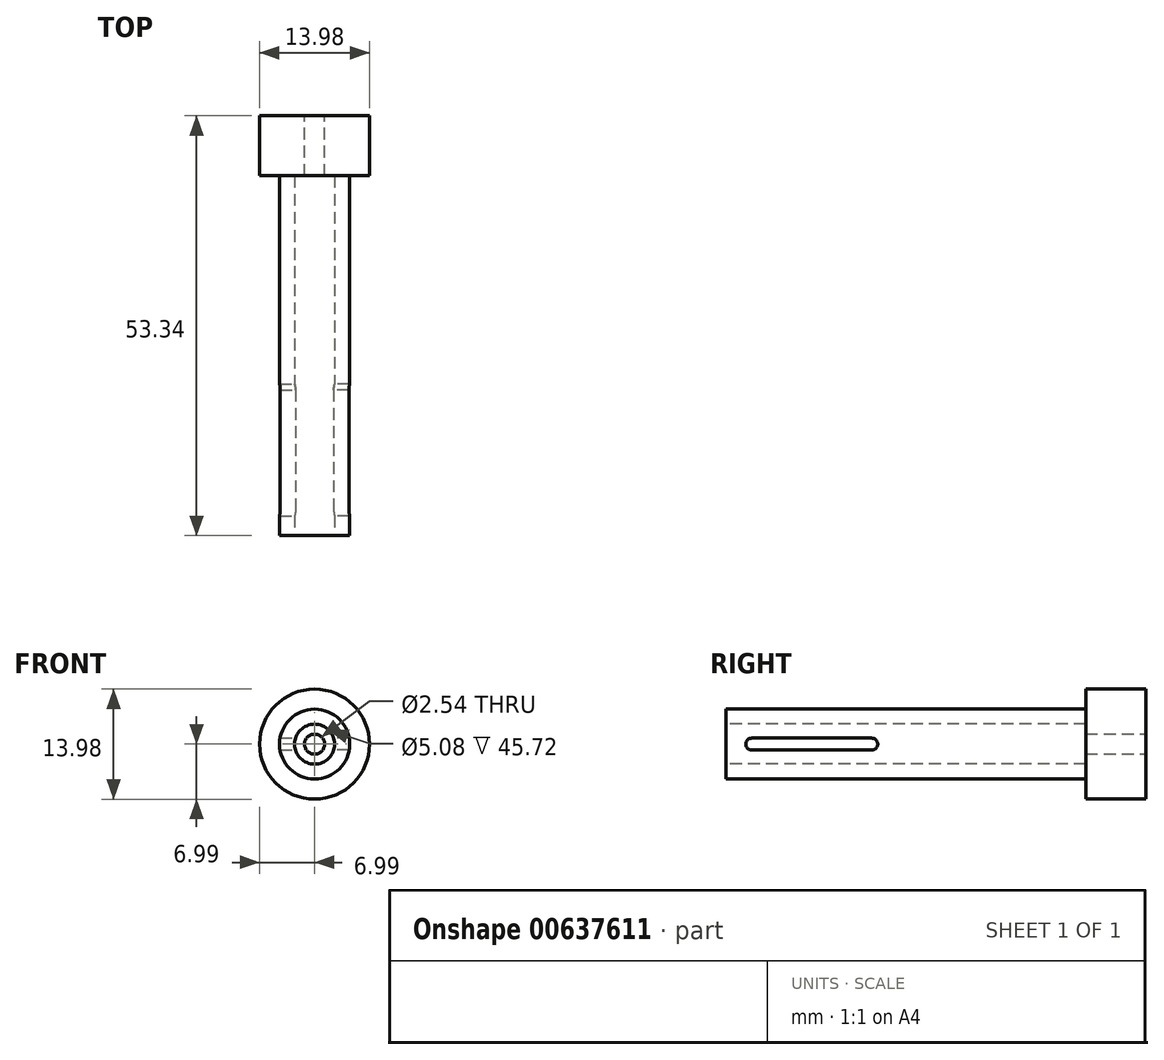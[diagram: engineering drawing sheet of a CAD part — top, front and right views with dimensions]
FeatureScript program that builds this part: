
annotation { "Feature Type Name" : "Feature", "Feature Type Description" : "" }
export const myFeature = defineFeature(function(context is Context, id is Id, definition is map)
    precondition{}
    {
        {
            var Q0;
            Q0=qCreatedBy(makeId("Front.planeOp"),FACE);
            var sketch = newSketch(context, id + "F0", { "sketchPlane" : qUnion([Q0])});
            skCircle(sketch, "E0", {"center": v(0, 0) * mm, "radius": 6.99 * mm});
            skCircle(sketch, "E1", {"center": v(0, 0) * mm, "radius": 1.27 * mm});
            skSolve(sketch);
        }
        {
            var Q0;
            Q0=qSketchRegion(id+"F0",true);
            var Q1;
            Q1=makeQuery(id+"F0.imprint","IMPRINT",FACE,{"disambiguationData":[TD([[makeQuery(id+"F0.imprint","IMPRINT",EDGE,{"derivedFrom":sQuery(id+"F0.wireOp",EDGE,"E0")}),1.0]])]});
            extrude(context, id + "F1", {"entities" : qUnion([Q0, Q1]), "depth" : 7.62 * mm});
        }
        {
            var Q0;
            Q0=makeQuery(id+"F1.opExtrude","CAP_FACE",FACE,{"disambiguationData":[OSD([sQuery(id+"F0.wireOp",EDGE,"E0"),sQuery(id+"F0.wireOp",EDGE,"E1")])],"isStart":false});
            var sketch = newSketch(context, id + "F2", { "sketchPlane" : qUnion([Q0])});
            skCircle(sketch, "E2", {"center": v(0, 0) * mm, "radius": 4.45 * mm});
            skSolve(sketch);
        }
        {
            var Q0;
            Q0=makeQuery(id+"F2.imprint","IMPRINT",FACE,{"disambiguationData":[TD([[makeQuery(id+"F2.imprint","IMPRINT",EDGE,{"derivedFrom":sQuery(id+"F2.wireOp",EDGE,"E2")}),1.0]])]});
            extrude(context, id + "F3", {"entities" : qUnion([Q0]), "operationType" : NewBodyOperationType.ADD, "depth" : 45.72 * mm});
        }
        {
            var Q0;
            Q0=qCreatedBy(makeId("Right.planeOp"),FACE);
            var sketch = newSketch(context, id + "F4", { "sketchPlane" : qUnion([Q0])});
            skLineSegment(sketch, "E3", {"start": v(-53.35, 0) * mm, "end": v(-50.81, 0) * mm});
            skLineSegment(sketch, "E4", {"start": v(-50.81, 0) * mm, "end": v(-34.05, 0) * mm});
            skCircle(sketch, "E5", {"center": v(-34.81, 0) * mm, "radius": 0.76 * mm});
            skCircle(sketch, "E6", {"center": v(-50.05, 0) * mm, "radius": 0.76 * mm});
            skLineSegment(sketch, "E7", {"start": v(-34.83, 0.76) * mm, "end": v(-50.05, 0.76) * mm});
            skLineSegment(sketch, "E8", {"start": v(-50.05, 0.76) * mm, "end": v(-50.05, -0.76) * mm});
            skLineSegment(sketch, "E9", {"start": v(-50.05, -0.76) * mm, "end": v(-34.81, -0.76) * mm});
            skSolve(sketch);
        }
        {
            var Q0;
            Q0=qSketchRegion(id+"F4",true);
            extrude(context, id + "F5", {"entities" : qUnion([Q0]), "operationType" : NewBodyOperationType.REMOVE, "oppositeDirection" : true, "depth" : 25.4 * mm});
        }
        {
            var Q0;
            Q0=qSketchRegion(id+"F4",true);
            extrude(context, id + "F6", {"entities" : qUnion([Q0]), "operationType" : NewBodyOperationType.REMOVE, "depth" : 25.4 * mm});
        }
        {
            var Q0;
            Q0=makeQuery(id+"F3.opExtrude","CAP_FACE",FACE,{"disambiguationData":[OSD([sQuery(id+"F0.wireOp",EDGE,"E1"),sQuery(id+"F2.wireOp",EDGE,"E2")])],"isStart":false});
            var sketch = newSketch(context, id + "F7", { "sketchPlane" : qUnion([Q0])});
            skCircle(sketch, "E10", {"center": v(0, 0) * mm, "radius": 2.54 * mm});
            skSolve(sketch);
        }
        {
            var Q0;
            Q0=makeQuery(id+"F7.imprint","IMPRINT",FACE,{"disambiguationData":[TD([[makeQuery(id+"F7.imprint","IMPRINT",EDGE,{"derivedFrom":sQuery(id+"F7.wireOp",EDGE,"E10")}),1.0]])]});
            extrude(context, id + "F8", {"entities" : qUnion([Q0]), "operationType" : NewBodyOperationType.REMOVE, "oppositeDirection" : true, "depth" : 20.32 * mm});
        }
        {
            var Q0;
            Q0=makeQuery(id+"F8.boolean.opBoolean","COPY",FACE,{"derivedFrom":makeQuery(id+"F8.opExtrude","CAP_FACE",FACE,{"disambiguationData":[OSD([sQuery(id+"F0.wireOp",EDGE,"E1"),sQuery(id+"F7.wireOp",EDGE,"E10")])],"isStart":false})});
            extrude(context, id + "F9", {"entities" : qUnion([Q0]), "operationType" : NewBodyOperationType.REMOVE, "oppositeDirection" : true, "depth" : 25.4 * mm});
        }
    });
